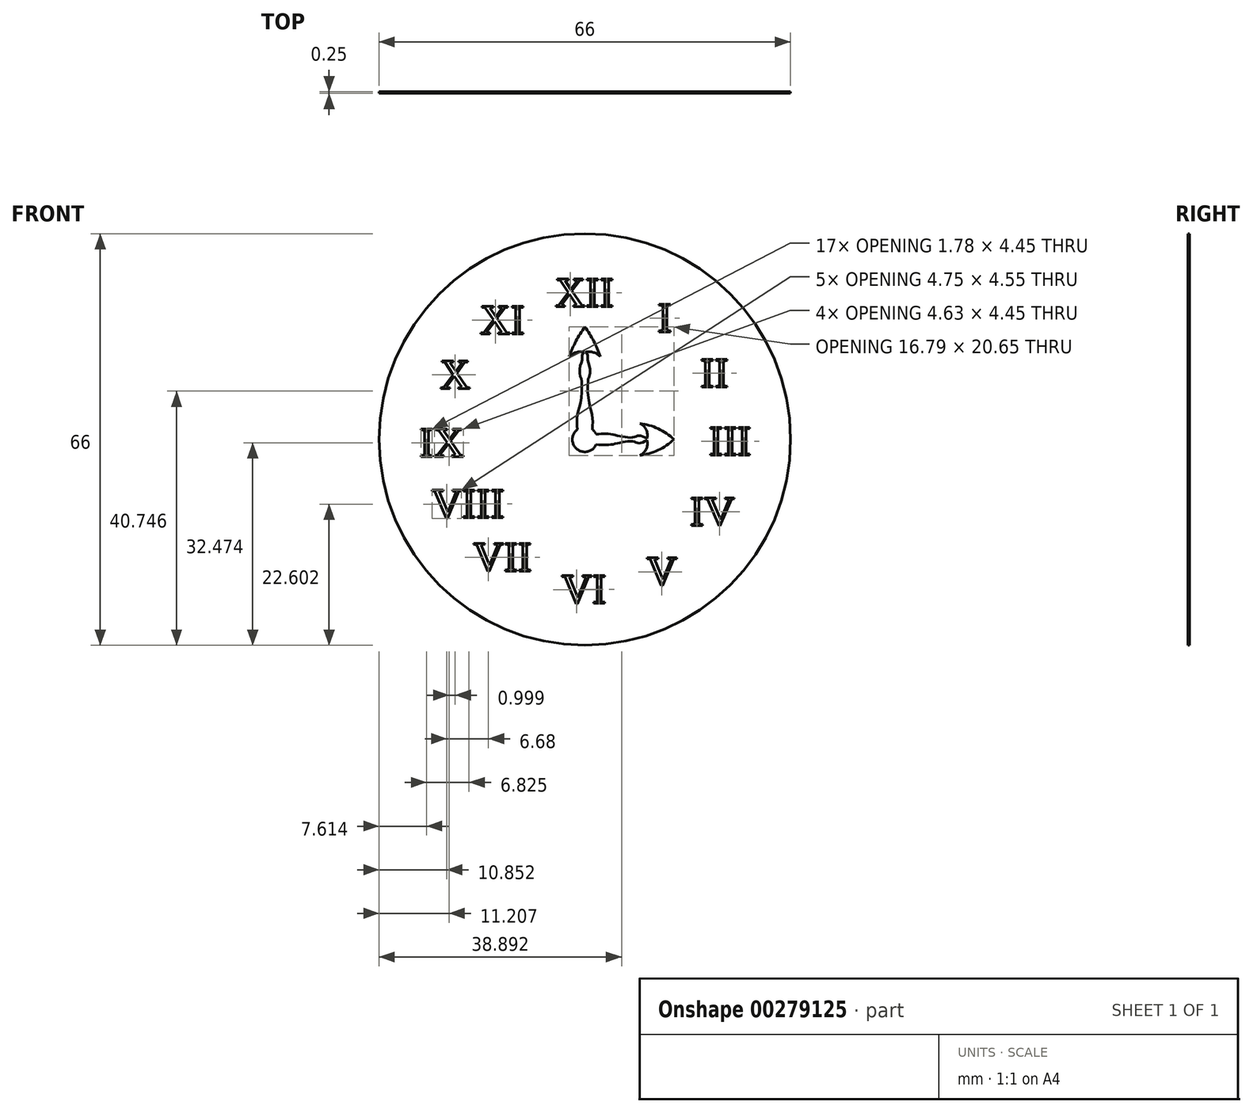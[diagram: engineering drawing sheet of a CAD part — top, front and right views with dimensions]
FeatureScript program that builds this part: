
annotation { "Feature Type Name" : "Feature", "Feature Type Description" : "" }
export const myFeature = defineFeature(function(context is Context, id is Id, definition is map)
    precondition{}
    {
        {
            var Q0;
            Q0=qCreatedBy(makeId("Front.planeOp"),FACE);
            var sketch = newSketch(context, id + "F0", { "sketchPlane" : qUnion([Q0])});
            skCircle(sketch, "E0", {"center": v(0, 0) * mm, "radius": 33 * mm});
            skSolve(sketch);
        }
        {
            var Q0;
            Q0=makeQuery(id+"F0.imprint","IMPRINT",FACE,{"disambiguationData":[TD([[makeQuery(id+"F0.imprint","IMPRINT",EDGE,{"derivedFrom":sQuery(id+"F0.wireOp",EDGE,"E0")}),1.0]])]});
            var sketch = newSketch(context, id + "F1", { "sketchPlane" : qUnion([Q0])});
            skText(sketch, "E1", { "text": "XII", "fontName": "Tinos-Regular.ttf"});
            const initialGuessF1  = {"E1": [-0.0048, 0.02129, 1, 0, 0.00489]};
            skSetInitialGuess(sketch, initialGuessF1);
            skSolve(sketch);
        }
        {
            var Q0;
            Q0=makeQuery(id+"F0.imprint","IMPRINT",FACE,{"disambiguationData":[TD([[makeQuery(id+"F0.imprint","IMPRINT",EDGE,{"derivedFrom":sQuery(id+"F0.wireOp",EDGE,"E0")}),1.0]])]});
            var sketch = newSketch(context, id + "F2", { "sketchPlane" : qUnion([Q0])});
            skText(sketch, "E2", { "text": "III", "fontName": "Tinos-Regular.ttf"});
            const initialGuessF2  = {"E2": [0.01991, -0.00252, 1, 0, 0.00489]};
            skSetInitialGuess(sketch, initialGuessF2);
            skSolve(sketch);
        }
        {
            var Q0;
            Q0=makeQuery(id+"F0.imprint","IMPRINT",FACE,{"disambiguationData":[TD([[makeQuery(id+"F0.imprint","IMPRINT",EDGE,{"derivedFrom":sQuery(id+"F0.wireOp",EDGE,"E0")}),1.0]])]});
            var sketch = newSketch(context, id + "F3", { "sketchPlane" : qUnion([Q0])});
            skText(sketch, "E3", { "text": "VI", "fontName": "Tinos-Regular.ttf"});
            const initialGuessF3  = {"E3": [-0.00374, -0.02628, 1, 0, 0.00489]};
            skSetInitialGuess(sketch, initialGuessF3);
            skSolve(sketch);
        }
        {
            var Q0;
            Q0=makeQuery(id+"F0.imprint","IMPRINT",FACE,{"disambiguationData":[TD([[makeQuery(id+"F0.imprint","IMPRINT",EDGE,{"derivedFrom":sQuery(id+"F0.wireOp",EDGE,"E0")}),1.0]])]});
            var sketch = newSketch(context, id + "F4", { "sketchPlane" : qUnion([Q0])});
            skText(sketch, "E4", { "text": "IX", "fontName": "Tinos-Regular.ttf"});
            const initialGuessF4  = {"E4": [-0.02652, -0.00275, 1, 0, 0.00489]};
            skSetInitialGuess(sketch, initialGuessF4);
            skSolve(sketch);
        }
        {
            var Q0;
            Q0=qCreatedBy(makeId("Front.planeOp"),FACE);
            var sketch = newSketch(context, id + "F5", { "sketchPlane" : qUnion([Q0])});
            skText(sketch, "E5", { "text": "I", "fontName": "Tinos-Regular.ttf"});
            const initialGuessF5  = {"E5": [0.01168, 0.01725, 1, 0, 0.00489]};
            skSetInitialGuess(sketch, initialGuessF5);
            skSolve(sketch);
        }
        {
            var Q0;
            Q0=makeQuery(id+"F0.imprint","IMPRINT",FACE,{"disambiguationData":[TD([[makeQuery(id+"F0.imprint","IMPRINT",EDGE,{"derivedFrom":sQuery(id+"F0.wireOp",EDGE,"E0")}),1.0]])]});
            var sketch = newSketch(context, id + "F6", { "sketchPlane" : qUnion([Q0])});
            skText(sketch, "E6", { "text": "II", "fontName": "Tinos-Regular.ttf"});
            const initialGuessF6  = {"E6": [0.01852, 0.00837, 1, 0, 0.00489]};
            skSetInitialGuess(sketch, initialGuessF6);
            skSolve(sketch);
        }
        {
            var Q0;
            Q0=makeQuery(id+"F0.imprint","IMPRINT",FACE,{"disambiguationData":[TD([[makeQuery(id+"F0.imprint","IMPRINT",EDGE,{"derivedFrom":sQuery(id+"F0.wireOp",EDGE,"E0")}),1.0]])]});
            var sketch = newSketch(context, id + "F7", { "sketchPlane" : qUnion([Q0])});
            skSolve(sketch);
        }
        {
            var Q0;
            Q0=makeQuery(id+"F0.imprint","IMPRINT",FACE,{"disambiguationData":[TD([[makeQuery(id+"F0.imprint","IMPRINT",EDGE,{"derivedFrom":sQuery(id+"F0.wireOp",EDGE,"E0")}),1.0]])]});
            var sketch = newSketch(context, id + "F8", { "sketchPlane" : qUnion([Q0])});
            skText(sketch, "E7", { "text": "V", "fontName": "Tinos-Regular.ttf"});
            const initialGuessF8  = {"E7": [0.0099, -0.0234, 1, 0, 0.00489]};
            skSetInitialGuess(sketch, initialGuessF8);
            skSolve(sketch);
        }
        {
            var Q0;
            Q0=makeQuery(id+"F0.imprint","IMPRINT",FACE,{"disambiguationData":[TD([[makeQuery(id+"F0.imprint","IMPRINT",EDGE,{"derivedFrom":sQuery(id+"F0.wireOp",EDGE,"E0")}),1.0]])]});
            var sketch = newSketch(context, id + "F9", { "sketchPlane" : qUnion([Q0])});
            skText(sketch, "E8", { "text": "IV", "fontName": "Tinos-Regular.ttf"});
            const initialGuessF9  = {"E8": [0.01688, -0.0138, 1, 0, 0.00489]};
            skSetInitialGuess(sketch, initialGuessF9);
            skSolve(sketch);
        }
        {
            var Q0;
            Q0=makeQuery(id+"F0.imprint","IMPRINT",FACE,{"disambiguationData":[TD([[makeQuery(id+"F0.imprint","IMPRINT",EDGE,{"derivedFrom":sQuery(id+"F0.wireOp",EDGE,"E0")}),1.0]])]});
            var sketch = newSketch(context, id + "F10", { "sketchPlane" : qUnion([Q0])});
            skText(sketch, "E9", { "text": "VII", "fontName": "Tinos-Regular.ttf"});
            const initialGuessF10  = {"E9": [-0.01792, -0.0211, 1, 0, 0.00489]};
            skSetInitialGuess(sketch, initialGuessF10);
            skSolve(sketch);
        }
        {
            var Q0;
            Q0=makeQuery(id+"F0.imprint","IMPRINT",FACE,{"disambiguationData":[TD([[makeQuery(id+"F0.imprint","IMPRINT",EDGE,{"derivedFrom":sQuery(id+"F0.wireOp",EDGE,"E0")}),1.0]])]});
            var sketch = newSketch(context, id + "F11", { "sketchPlane" : qUnion([Q0])});
            skText(sketch, "E10", { "text": "VIII", "fontName": "Tinos-Regular.ttf"});
            const initialGuessF11  = {"E10": [-0.0246, -0.01257, 1, 0, 0.00489]};
            skSetInitialGuess(sketch, initialGuessF11);
            skSolve(sketch);
        }
        {
            var Q0;
            Q0=makeQuery(id+"F0.imprint","IMPRINT",FACE,{"disambiguationData":[TD([[makeQuery(id+"F0.imprint","IMPRINT",EDGE,{"derivedFrom":sQuery(id+"F0.wireOp",EDGE,"E0")}),1.0]])]});
            var sketch = newSketch(context, id + "F12", { "sketchPlane" : qUnion([Q0])});
            skText(sketch, "E11", { "text": "X", "fontName": "Tinos-Regular.ttf"});
            const initialGuessF12  = {"E11": [-0.02326, 0.00812, 1, 0, 0.00489]};
            skSetInitialGuess(sketch, initialGuessF12);
            skSolve(sketch);
        }
        {
            var Q0;
            Q0=makeQuery(id+"F0.imprint","IMPRINT",FACE,{"disambiguationData":[TD([[makeQuery(id+"F0.imprint","IMPRINT",EDGE,{"derivedFrom":sQuery(id+"F0.wireOp",EDGE,"E0")}),1.0]])]});
            var sketch = newSketch(context, id + "F13", { "sketchPlane" : qUnion([Q0])});
            skText(sketch, "E12", { "text": "XI", "fontName": "Tinos-Regular.ttf"});
            const initialGuessF13  = {"E12": [-0.01683, 0.01691, 1, 0, 0.00489]};
            skSetInitialGuess(sketch, initialGuessF13);
            skSolve(sketch);
        }
        {
            var Q0;
            Q0 = qSketchRegion(id + "F0", true);
            extrude(context, id + "F14", {"entities" : qUnion([Q0]), "depth" : .25 * mm});
        }
        {
            var Q0;
            Q0 = qSketchRegion(id + "F9", true);
            extrude(context, id + "F15", {"entities" : qUnion([Q0]), "operationType" : NewBodyOperationType.REMOVE, "depth" : 25 * mm});
        }
        {
            var Q0;
            Q0 = qSketchRegion(id + "F10", true);
            extrude(context, id + "F16", {"entities" : qUnion([Q0]), "operationType" : NewBodyOperationType.REMOVE, "depth" : 25 * mm});
        }
        {
            var Q0;
            Q0 = qSketchRegion(id + "F11", true);
            extrude(context, id + "F17", {"entities" : qUnion([Q0]), "operationType" : NewBodyOperationType.REMOVE, "depth" : 25 * mm});
        }
        {
            var Q0;
            Q0 = qSketchRegion(id + "F12", true);
            extrude(context, id + "F18", {"entities" : qUnion([Q0]), "operationType" : NewBodyOperationType.REMOVE, "depth" : 25 * mm});
        }
        {
            var Q0;
            Q0 = qSketchRegion(id + "F13", true);
            extrude(context, id + "F19", {"entities" : qUnion([Q0]), "operationType" : NewBodyOperationType.REMOVE, "depth" : 25 * mm});
        }
        {
            var Q0;
            Q0 = qSketchRegion(id + "F1", true);
            var Q1;
            Q1 = qSketchRegion(id + "F2", true);
            var Q2;
            Q2 = qSketchRegion(id + "F3", true);
            var Q3;
            Q3 = qSketchRegion(id + "F4", true);
            var Q4;
            Q4 = qSketchRegion(id + "F5", true);
            var Q5;
            Q5 = qSketchRegion(id + "F6", true);
            var Q6;
            Q6 = qSketchRegion(id + "F7", true);
            var Q7;
            Q7 = qSketchRegion(id + "F8", true);
            extrude(context, id + "F20", {"entities" : qUnion([Q0, Q1, Q2, Q3, Q4, Q5, Q6, Q7]), "operationType" : NewBodyOperationType.REMOVE, "depth" : 25 * mm});
        }
        {
            var Q0;
            Q0=makeQuery(id+"F14.opExtrude","CAP_FACE",FACE,{"disambiguationData":[OSD([sQuery(id+"F0.wireOp",EDGE,"E0")])],"isStart":false});
            var sketch = newSketch(context, id + "F21", { "sketchPlane" : qUnion([Q0])});
            skCircle(sketch, "E13", {"center": v(0, 0) * mm, "radius": 2 * mm});
            skFitSpline(sketch, "E14", {"points": [v(-1.2, 1.6) * mm, v(-1.2, 3.81) * mm, v(-0.55, 6.74) * mm, v(-0.59, 9.84) * mm, v(-0.62, 9.84) * mm, v(-0.84, 11.25) * mm, v(-0.44, 12.8) * mm, v(-0.4, 13.63) * mm, v(0, 14.06) * mm], "startDerivative": vector(-1.14, 13.96) * mm, "endDerivative": vector(6.22, 4.53) * mm});
            skFitSpline(sketch, "E15.MirrorCS", {"points": [v(1.2, 1.6) * mm, v(1.2, 3.81) * mm, v(0.55, 6.74) * mm, v(0.59, 9.84) * mm, v(0.62, 9.84) * mm, v(0.84, 11.25) * mm, v(0.44, 12.8) * mm, v(0.4, 13.63) * mm, v(0, 14.06) * mm], "startDerivative": vector(1.14, 13.96) * mm, "endDerivative": vector(-6.22, 4.53) * mm});
            skFitSpline(sketch, "E16", {"points": [v(1.82, 0.82) * mm, v(3.85, 0.87) * mm, v(5.73, 0.51) * mm, v(7.82, 0.34) * mm, v(8.74, 0.6) * mm, v(10.18, 0) * mm], "startDerivative": vector(9.46, 0.73) * mm, "endDerivative": vector(8.12, -4.73) * mm});
            skFitSpline(sketch, "E17.MirrorCS", {"points": [v(1.82, -0.82) * mm, v(3.85, -0.87) * mm, v(5.73, -0.51) * mm, v(7.82, -0.34) * mm, v(8.74, -0.6) * mm, v(10.18, 0) * mm], "startDerivative": vector(9.46, -0.73) * mm, "endDerivative": vector(8.12, 4.73) * mm});
            skSolve(sketch);
        }
        {
            var Q0;
            Q0 = qSketchRegion(id + "F21", true);
            extrude(context, id + "F22", {"entities" : qUnion([Q0]), "operationType" : NewBodyOperationType.REMOVE, "oppositeDirection" : true, "depth" : 25 * mm});
        }
        {
            var Q0;
            Q0=makeQuery(id+"F14.opExtrude","CAP_FACE",FACE,{"disambiguationData":[OSD([sQuery(id+"F0.wireOp",EDGE,"E0")])],"isStart":false});
            var sketch = newSketch(context, id + "F23", { "sketchPlane" : qUnion([Q0])});
            skArc(sketch, "E18", {"start": v(14.29, 0) * mm, "mid": v(11.76, 1.72) * mm, "end": v(8.82, 2.58) * mm});
            skArc(sketch, "E19.MirrorCS", {"start": v(14.29, 0) * mm, "mid": v(11.76, -1.72) * mm, "end": v(8.82, -2.58) * mm});
            skArc(sketch, "E20.MirrorCS", {"start": v(9.9, 0) * mm, "mid": v(9.87, -1.5) * mm, "end": v(8.82, -2.58) * mm});
            skArc(sketch, "E21", {"start": v(0, 18.07) * mm, "mid": v(-1.42, 15.76) * mm, "end": v(-2.5, 13.27) * mm});
            skArc(sketch, "E22.MirrorCS", {"start": v(0, 18.07) * mm, "mid": v(1.42, 15.76) * mm, "end": v(2.5, 13.27) * mm});
            skArc(sketch, "E23.MirrorCS", {"start": v(0, 13.96) * mm, "mid": v(1.35, 13.97) * mm, "end": v(2.5, 13.27) * mm});
            skArc(sketch, "E24.MirrorCS", {"start": v(0, 13.96) * mm, "mid": v(-1.35, 13.97) * mm, "end": v(-2.5, 13.27) * mm});
            skArc(sketch, "E25.MirrorCS", {"start": v(9.9, 0) * mm, "mid": v(9.87, 1.5) * mm, "end": v(8.82, 2.58) * mm});
            skSolve(sketch);
        }
        {
            var Q0;
            Q0 = qSketchRegion(id + "F23", true);
            extrude(context, id + "F24", {"entities" : qUnion([Q0]), "operationType" : NewBodyOperationType.REMOVE, "oppositeDirection" : true, "depth" : 25 * mm});
        }
    });
